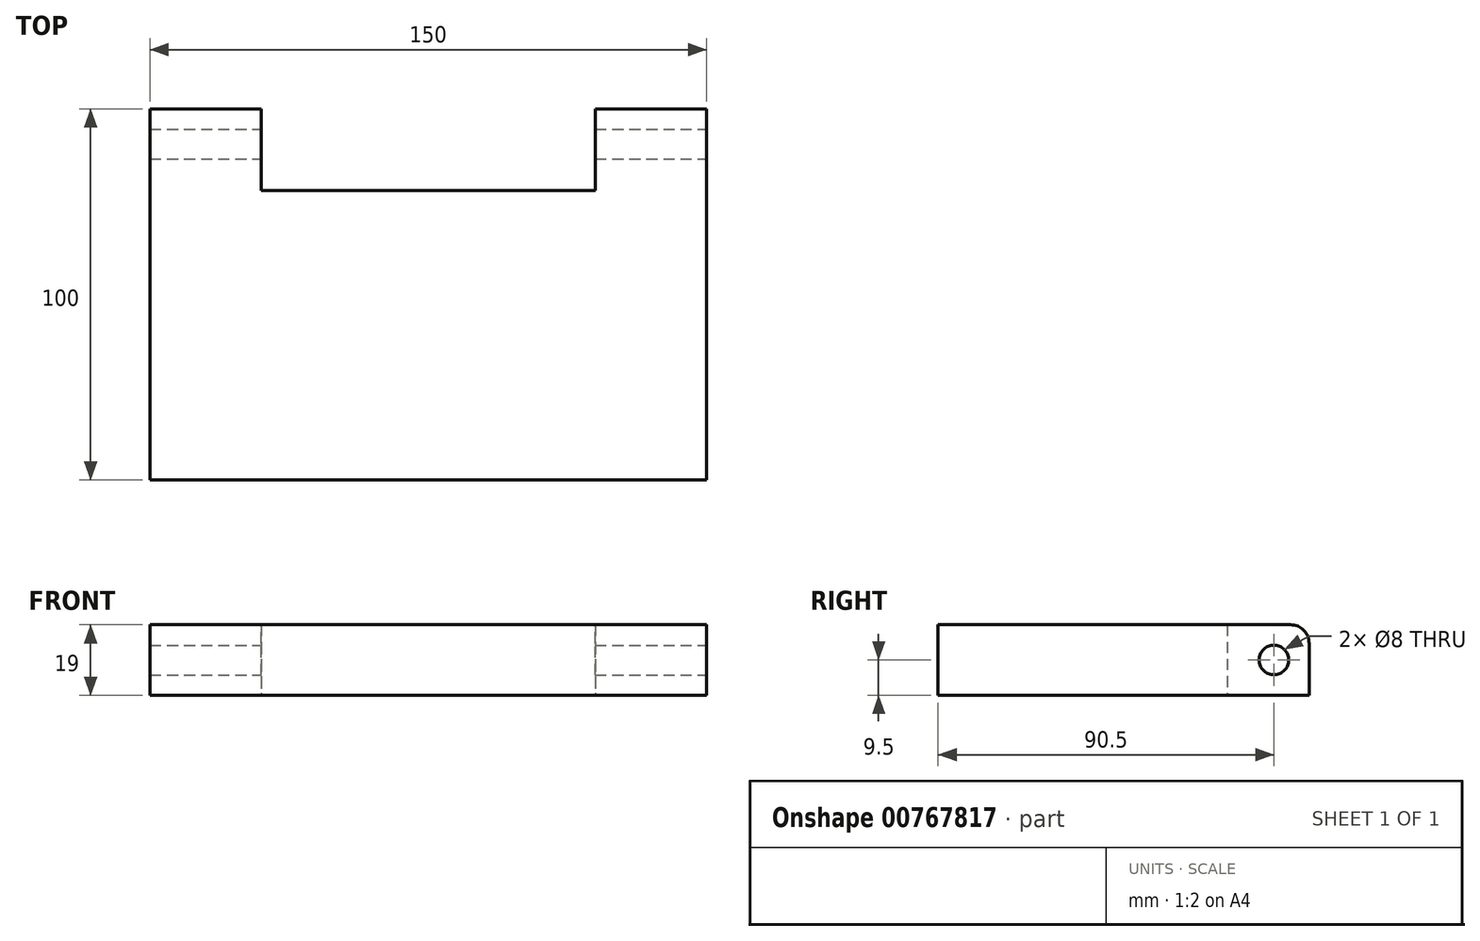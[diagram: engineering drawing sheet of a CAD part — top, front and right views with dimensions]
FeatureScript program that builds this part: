
annotation { "Feature Type Name" : "Feature", "Feature Type Description" : "" }
export const myFeature = defineFeature(function(context is Context, id is Id, definition is map)
    precondition{}
    {
        {
            var Q0;
            Q0=qCreatedBy(makeId("Top.planeOp"),FACE);
            var sketch = newSketch(context, id + "F0", { "sketchPlane" : qUnion([Q0])});
            skLineSegment(sketch, "E0.bottom", {"start": v(75, -50) * mm, "end": v(-75, -50) * mm});
            skLineSegment(sketch, "E0.top", {"start": v(75, 50) * mm, "end": v(45, 50) * mm});
            skLineSegment(sketch, "E0.left", {"start": v(75, -50) * mm, "end": v(75, 50) * mm});
            skLineSegment(sketch, "E0.right", {"start": v(-75, -50) * mm, "end": v(-75, 50) * mm});
            skPoint(sketch, "E0.middle", {"position": v(0, 0) * mm});
            skLineSegment(sketch, "E1.top", {"start": v(-45, 28) * mm, "end": v(45, 28) * mm});
            skLineSegment(sketch, "E1.left", {"start": v(-45, 50) * mm, "end": v(-45, 28) * mm});
            skLineSegment(sketch, "E1.right", {"start": v(45, 50) * mm, "end": v(45, 28) * mm});
            skLineSegment(sketch, "E2.trimOffspring", {"start": v(-45, 50) * mm, "end": v(-75, 50) * mm});
            skSolve(sketch);
        }
        {
            var Q0;
            Q0=makeQuery(id+"F0.imprint","IMPRINT",FACE,{"disambiguationData":[TD([[makeQuery(id+"F0.imprint","IMPRINT",EDGE,{"derivedFrom":sQuery(id+"F0.wireOp",EDGE,"E0.bottom")}),-1.0]])]});
            extrude(context, id + "F1", {"entities" : qUnion([Q0]), "depth" : 19 * mm, "offsetDistance" : 25 * mm});
        }
        {
            var Q0;
            Q0=makeQuery(id+"F1.opExtrude","SWEPT_FACE",FACE,{"disambiguationData":[OSD([sQuery(id+"F0.wireOp",EDGE,"E0.left")])]});
            var sketch = newSketch(context, id + "F2", { "sketchPlane" : qUnion([Q0])});
            skLineSegment(sketch, "E3", {"start": v(31, 19) * mm, "end": v(31, 0) * mm, "construction": true});
            skLineSegment(sketch, "E4", {"start": v(31, 19) * mm, "end": v(50, 0) * mm, "construction": true});
            skCircle(sketch, "E5", {"center": v(40.5, 9.5) * mm, "radius": 4 * mm});
            skSolve(sketch);
        }
        {
            var Q0;
            Q0=makeQuery(id+"F2.imprint","IMPRINT",FACE,{"disambiguationData":[TD([[makeQuery(id+"F2.imprint","IMPRINT",EDGE,{"derivedFrom":sQuery(id+"F2.wireOp",EDGE,"E5")}),1.0]])]});
            extrude(context, id + "F3", {"entities" : qUnion([Q0]), "operationType" : NewBodyOperationType.REMOVE, "endBound" : BoundingType.THROUGH_ALL, "oppositeDirection" : true, "depth" : 25 * mm, "offsetDistance" : 25 * mm});
        }
        {
            var Q0;
            Q0=makeQuery(id+"F1.opExtrude","CAP_EDGE",EDGE,{"disambiguationData":[OSD([sQuery(id+"F0.wireOp",EDGE,"E2.trimOffspring")])],"isStart":false});
            var Q1;
            Q1=makeQuery(id+"F1.opExtrude","CAP_EDGE",EDGE,{"disambiguationData":[OSD([sQuery(id+"F0.wireOp",EDGE,"E0.top")])],"isStart":false});
            fillet(context, id + "F4", {"entities" : qUnion([Q0, Q1]), "radius" : 5 * mm, "tangentPropagation" : true, "allowEdgeOverflow" : false});
        }
    });
